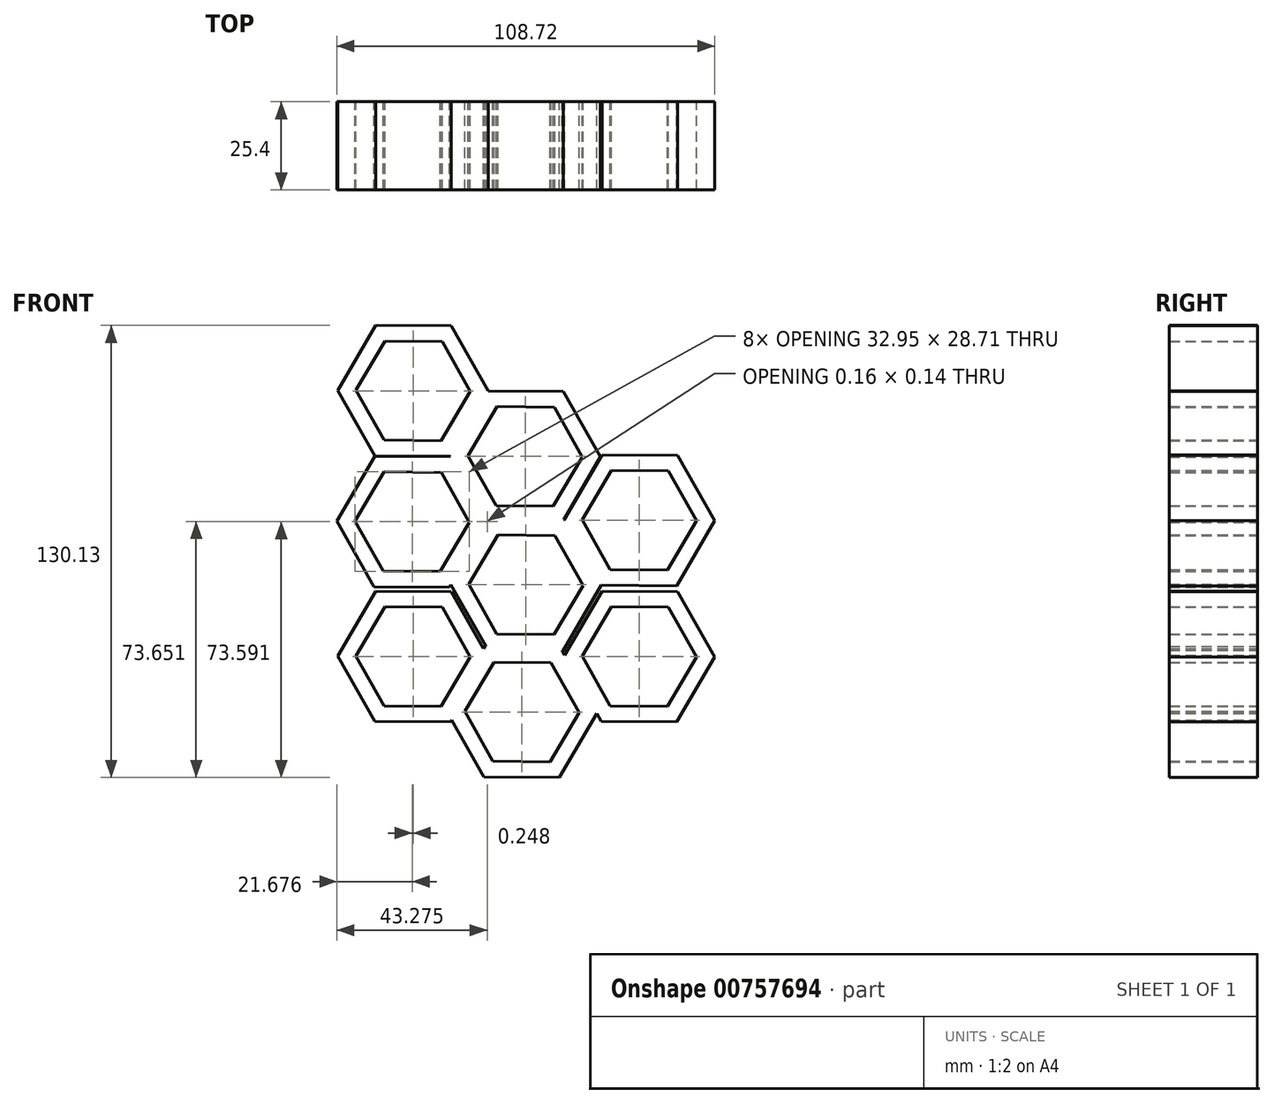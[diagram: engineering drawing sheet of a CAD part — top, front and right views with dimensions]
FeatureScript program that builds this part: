
annotation { "Feature Type Name" : "Feature", "Feature Type Description" : "" }
export const myFeature = defineFeature(function(context is Context, id is Id, definition is map)
    precondition{}
    {
        {
            var Q0;
            Q0=qCreatedBy(makeId("Front.planeOp"),FACE);
            var sketch = newSketch(context, id + "F0", { "sketchPlane" : qUnion([Q0])});
            skCircle(sketch, "E0.cCircle", {"center": v(-59.12, 45.17) * mm, "radius": 18.77 * mm, "construction": true});
            skLineSegment(sketch, "E0.0", {"start": v(-37.45, 45.03) * mm, "end": v(-48.41, 26.33) * mm});
            skLineSegment(sketch, "E0.1", {"start": v(-48.41, 26.33) * mm, "end": v(-70.09, 26.47) * mm});
            skLineSegment(sketch, "E0.2", {"start": v(-70.09, 26.47) * mm, "end": v(-80.8, 45.31) * mm});
            skLineSegment(sketch, "E0.3", {"start": v(-80.8, 45.31) * mm, "end": v(-69.84, 64.01) * mm});
            skLineSegment(sketch, "E0.4", {"start": v(-69.84, 64.01) * mm, "end": v(-48.16, 63.87) * mm});
            skLineSegment(sketch, "E0.5", {"start": v(-48.16, 63.87) * mm, "end": v(-37.45, 45.03) * mm});
            skPoint(sketch, "E0.0.midPoint", {"position": v(-42.93, 35.68) * mm});
            skCircle(sketch, "E1.cCircle", {"center": v(-59.12, 45.17) * mm, "radius": 14.27 * mm, "construction": true});
            skLineSegment(sketch, "E1.0", {"start": v(-42.65, 45) * mm, "end": v(-51.03, 30.82) * mm});
            skLineSegment(sketch, "E1.1", {"start": v(-51.03, 30.82) * mm, "end": v(-67.5, 30.98) * mm});
            skLineSegment(sketch, "E1.2", {"start": v(-67.5, 30.98) * mm, "end": v(-75.6, 45.34) * mm});
            skLineSegment(sketch, "E1.3", {"start": v(-75.6, 45.34) * mm, "end": v(-67.22, 59.52) * mm});
            skLineSegment(sketch, "E1.4", {"start": v(-67.22, 59.52) * mm, "end": v(-50.74, 59.36) * mm});
            skLineSegment(sketch, "E1.5", {"start": v(-50.74, 59.36) * mm, "end": v(-42.65, 45) * mm});
            skPoint(sketch, "E1.0.midPoint", {"position": v(-46.84, 37.91) * mm});
            skCircle(sketch, "E2.cCircle", {"center": v(-26.64, 64) * mm, "radius": 18.77 * mm, "construction": true});
            skLineSegment(sketch, "E2.0", {"start": v(-4.97, 63.86) * mm, "end": v(-15.93, 45.16) * mm});
            skLineSegment(sketch, "E2.1", {"start": v(-15.93, 45.16) * mm, "end": v(-37.6, 45.3) * mm});
            skLineSegment(sketch, "E2.2", {"start": v(-37.6, 45.3) * mm, "end": v(-48.32, 64.14) * mm});
            skLineSegment(sketch, "E2.3", {"start": v(-48.32, 64.14) * mm, "end": v(-37.35, 82.84) * mm});
            skLineSegment(sketch, "E2.4", {"start": v(-37.35, 82.84) * mm, "end": v(-15.68, 82.7) * mm});
            skLineSegment(sketch, "E2.5", {"start": v(-15.68, 82.7) * mm, "end": v(-4.97, 63.86) * mm});
            skPoint(sketch, "E2.0.midPoint", {"position": v(-10.45, 54.5) * mm});
            skCircle(sketch, "E3.cCircle", {"center": v(-26.64, 64) * mm, "radius": 14.27 * mm, "construction": true});
            skLineSegment(sketch, "E3.0", {"start": v(-10.16, 63.83) * mm, "end": v(-18.55, 49.65) * mm});
            skLineSegment(sketch, "E3.1", {"start": v(-18.55, 49.65) * mm, "end": v(-35.02, 49.81) * mm});
            skLineSegment(sketch, "E3.2", {"start": v(-35.02, 49.81) * mm, "end": v(-43.12, 64.17) * mm});
            skLineSegment(sketch, "E3.3", {"start": v(-43.12, 64.17) * mm, "end": v(-34.74, 78.35) * mm});
            skLineSegment(sketch, "E3.4", {"start": v(-34.74, 78.35) * mm, "end": v(-18.26, 78.19) * mm});
            skLineSegment(sketch, "E3.5", {"start": v(-18.26, 78.19) * mm, "end": v(-10.16, 63.83) * mm});
            skPoint(sketch, "E3.0.midPoint", {"position": v(-14.36, 56.74) * mm});
            skCircle(sketch, "E4.cCircle", {"center": v(-26.4, 27.04) * mm, "radius": 18.77 * mm, "construction": true});
            skLineSegment(sketch, "E4.0", {"start": v(-4.72, 26.9) * mm, "end": v(-15.68, 8.2) * mm});
            skLineSegment(sketch, "E4.1", {"start": v(-15.68, 8.2) * mm, "end": v(-37.35, 8.34) * mm});
            skLineSegment(sketch, "E4.2", {"start": v(-37.35, 8.34) * mm, "end": v(-48.07, 27.18) * mm});
            skLineSegment(sketch, "E4.3", {"start": v(-48.07, 27.18) * mm, "end": v(-37.1, 45.88) * mm});
            skLineSegment(sketch, "E4.4", {"start": v(-37.1, 45.88) * mm, "end": v(-15.43, 45.73) * mm});
            skLineSegment(sketch, "E4.5", {"start": v(-15.43, 45.73) * mm, "end": v(-4.72, 26.9) * mm});
            skPoint(sketch, "E4.0.midPoint", {"position": v(-10.2, 17.54) * mm});
            skCircle(sketch, "E5.cCircle", {"center": v(-26.4, 27.04) * mm, "radius": 14.27 * mm, "construction": true});
            skLineSegment(sketch, "E5.0", {"start": v(-9.92, 26.87) * mm, "end": v(-18.3, 12.68) * mm});
            skLineSegment(sketch, "E5.1", {"start": v(-18.3, 12.68) * mm, "end": v(-34.78, 12.85) * mm});
            skLineSegment(sketch, "E5.2", {"start": v(-34.78, 12.85) * mm, "end": v(-42.87, 27.2) * mm});
            skLineSegment(sketch, "E5.3", {"start": v(-42.87, 27.2) * mm, "end": v(-34.49, 41.39) * mm});
            skLineSegment(sketch, "E5.4", {"start": v(-34.49, 41.39) * mm, "end": v(-18, 41.22) * mm});
            skLineSegment(sketch, "E5.5", {"start": v(-18, 41.22) * mm, "end": v(-9.92, 26.87) * mm});
            skPoint(sketch, "E5.0.midPoint", {"position": v(-14.1, 19.78) * mm});
            skCircle(sketch, "E6.cCircle", {"center": v(-58.88, 82.87) * mm, "radius": 18.77 * mm, "construction": true});
            skLineSegment(sketch, "E6.0", {"start": v(-37.2, 82.72) * mm, "end": v(-48.16, 64.02) * mm});
            skLineSegment(sketch, "E6.1", {"start": v(-48.16, 64.02) * mm, "end": v(-69.84, 64.17) * mm});
            skLineSegment(sketch, "E6.2", {"start": v(-69.84, 64.17) * mm, "end": v(-80.55, 83) * mm});
            skLineSegment(sketch, "E6.3", {"start": v(-80.55, 83) * mm, "end": v(-69.59, 101.7) * mm});
            skLineSegment(sketch, "E6.4", {"start": v(-69.59, 101.7) * mm, "end": v(-47.91, 101.57) * mm});
            skLineSegment(sketch, "E6.5", {"start": v(-47.91, 101.57) * mm, "end": v(-37.2, 82.72) * mm});
            skPoint(sketch, "E6.0.midPoint", {"position": v(-42.68, 73.37) * mm});
            skCircle(sketch, "E7.cCircle", {"center": v(-58.88, 82.87) * mm, "radius": 14.27 * mm, "construction": true});
            skLineSegment(sketch, "E7.0", {"start": v(-42.4, 82.7) * mm, "end": v(-50.78, 68.51) * mm});
            skLineSegment(sketch, "E7.1", {"start": v(-50.78, 68.51) * mm, "end": v(-67.26, 68.68) * mm});
            skLineSegment(sketch, "E7.2", {"start": v(-67.26, 68.68) * mm, "end": v(-75.35, 83.03) * mm});
            skLineSegment(sketch, "E7.3", {"start": v(-75.35, 83.03) * mm, "end": v(-66.97, 97.22) * mm});
            skLineSegment(sketch, "E7.4", {"start": v(-66.97, 97.22) * mm, "end": v(-50.5, 97.05) * mm});
            skLineSegment(sketch, "E7.5", {"start": v(-50.5, 97.05) * mm, "end": v(-42.4, 82.7) * mm});
            skPoint(sketch, "E7.0.midPoint", {"position": v(-46.6, 75.6) * mm});
            skCircle(sketch, "E8.cCircle", {"center": v(6.24, 45.6) * mm, "radius": 18.77 * mm, "construction": true});
            skLineSegment(sketch, "E8.0", {"start": v(27.92, 45.45) * mm, "end": v(16.96, 26.75) * mm});
            skLineSegment(sketch, "E8.1", {"start": v(16.96, 26.75) * mm, "end": v(-4.72, 26.9) * mm});
            skLineSegment(sketch, "E8.2", {"start": v(-4.72, 26.9) * mm, "end": v(-15.43, 45.73) * mm});
            skLineSegment(sketch, "E8.3", {"start": v(-15.43, 45.73) * mm, "end": v(-4.47, 64.43) * mm});
            skLineSegment(sketch, "E8.4", {"start": v(-4.47, 64.43) * mm, "end": v(17.2, 64.3) * mm});
            skLineSegment(sketch, "E8.5", {"start": v(17.2, 64.3) * mm, "end": v(27.92, 45.45) * mm});
            skPoint(sketch, "E8.0.midPoint", {"position": v(22.44, 36.1) * mm});
            skCircle(sketch, "E9.cCircle", {"center": v(6.24, 45.6) * mm, "radius": 14.27 * mm, "construction": true});
            skLineSegment(sketch, "E9.0", {"start": v(22.72, 45.42) * mm, "end": v(14.34, 31.24) * mm});
            skLineSegment(sketch, "E9.1", {"start": v(14.34, 31.24) * mm, "end": v(-2.14, 31.4) * mm});
            skLineSegment(sketch, "E9.2", {"start": v(-2.14, 31.4) * mm, "end": v(-10.23, 45.76) * mm});
            skLineSegment(sketch, "E9.3", {"start": v(-10.23, 45.76) * mm, "end": v(-1.85, 59.94) * mm});
            skLineSegment(sketch, "E9.4", {"start": v(-1.85, 59.94) * mm, "end": v(14.63, 59.78) * mm});
            skLineSegment(sketch, "E9.5", {"start": v(14.63, 59.78) * mm, "end": v(22.72, 45.42) * mm});
            skPoint(sketch, "E9.0.midPoint", {"position": v(18.53, 38.33) * mm});
            skCircle(sketch, "E10.cCircle", {"center": v(-58.88, 6.38) * mm, "radius": 18.77 * mm, "construction": true});
            skLineSegment(sketch, "E10.0", {"start": v(-37.2, 6.23) * mm, "end": v(-48.16, -12.47) * mm});
            skLineSegment(sketch, "E10.1", {"start": v(-48.16, -12.47) * mm, "end": v(-69.84, -12.32) * mm});
            skLineSegment(sketch, "E10.2", {"start": v(-69.84, -12.32) * mm, "end": v(-80.55, 6.52) * mm});
            skLineSegment(sketch, "E10.3", {"start": v(-80.55, 6.52) * mm, "end": v(-69.59, 25.22) * mm});
            skLineSegment(sketch, "E10.4", {"start": v(-69.59, 25.22) * mm, "end": v(-47.91, 25.08) * mm});
            skLineSegment(sketch, "E10.5", {"start": v(-47.91, 25.08) * mm, "end": v(-37.2, 6.23) * mm});
            skPoint(sketch, "E10.0.midPoint", {"position": v(-42.68, -3.12) * mm});
            skCircle(sketch, "E11.cCircle", {"center": v(-58.88, 6.38) * mm, "radius": 14.27 * mm, "construction": true});
            skLineSegment(sketch, "E11.0", {"start": v(-42.4, 6.2) * mm, "end": v(-50.78, -7.98) * mm});
            skLineSegment(sketch, "E11.1", {"start": v(-50.78, -7.98) * mm, "end": v(-67.26, -7.81) * mm});
            skLineSegment(sketch, "E11.2", {"start": v(-67.26, -7.81) * mm, "end": v(-75.35, 6.54) * mm});
            skLineSegment(sketch, "E11.3", {"start": v(-75.35, 6.54) * mm, "end": v(-66.97, 20.73) * mm});
            skLineSegment(sketch, "E11.4", {"start": v(-66.97, 20.73) * mm, "end": v(-50.5, 20.56) * mm});
            skLineSegment(sketch, "E11.5", {"start": v(-50.5, 20.56) * mm, "end": v(-42.4, 6.2) * mm});
            skPoint(sketch, "E11.0.midPoint", {"position": v(-46.6, -0.88) * mm});
            skCircle(sketch, "E12.cCircle", {"center": v(6.24, 6.38) * mm, "radius": 18.77 * mm, "construction": true});
            skLineSegment(sketch, "E12.0", {"start": v(27.92, 6.23) * mm, "end": v(16.96, -12.47) * mm});
            skLineSegment(sketch, "E12.1", {"start": v(16.96, -12.47) * mm, "end": v(-4.72, -12.32) * mm});
            skLineSegment(sketch, "E12.2", {"start": v(-4.72, -12.32) * mm, "end": v(-15.43, 6.52) * mm});
            skLineSegment(sketch, "E12.3", {"start": v(-15.43, 6.52) * mm, "end": v(-4.47, 25.22) * mm});
            skLineSegment(sketch, "E12.4", {"start": v(-4.47, 25.22) * mm, "end": v(17.2, 25.08) * mm});
            skLineSegment(sketch, "E12.5", {"start": v(17.2, 25.08) * mm, "end": v(27.92, 6.23) * mm});
            skPoint(sketch, "E12.0.midPoint", {"position": v(22.44, -3.12) * mm});
            skCircle(sketch, "E13.cCircle", {"center": v(6.24, 6.38) * mm, "radius": 14.27 * mm, "construction": true});
            skLineSegment(sketch, "E13.0", {"start": v(22.72, 6.2) * mm, "end": v(14.34, -7.98) * mm});
            skLineSegment(sketch, "E13.1", {"start": v(14.34, -7.98) * mm, "end": v(-2.14, -7.81) * mm});
            skLineSegment(sketch, "E13.2", {"start": v(-2.14, -7.81) * mm, "end": v(-10.23, 6.54) * mm});
            skLineSegment(sketch, "E13.3", {"start": v(-10.23, 6.54) * mm, "end": v(-1.85, 20.73) * mm});
            skLineSegment(sketch, "E13.4", {"start": v(-1.85, 20.73) * mm, "end": v(14.63, 20.56) * mm});
            skLineSegment(sketch, "E13.5", {"start": v(14.63, 20.56) * mm, "end": v(22.72, 6.2) * mm});
            skPoint(sketch, "E13.0.midPoint", {"position": v(18.53, -0.88) * mm});
            skCircle(sketch, "E14.cCircle", {"center": v(-27.54, -9.58) * mm, "radius": 18.77 * mm, "construction": true});
            skLineSegment(sketch, "E14.0", {"start": v(-5.87, -9.72) * mm, "end": v(-16.83, -28.42) * mm});
            skLineSegment(sketch, "E14.1", {"start": v(-16.83, -28.42) * mm, "end": v(-38.5, -28.28) * mm});
            skLineSegment(sketch, "E14.2", {"start": v(-38.5, -28.28) * mm, "end": v(-49.22, -9.43) * mm});
            skLineSegment(sketch, "E14.3", {"start": v(-49.22, -9.43) * mm, "end": v(-38.26, 9.27) * mm});
            skLineSegment(sketch, "E14.4", {"start": v(-38.26, 9.27) * mm, "end": v(-16.58, 9.12) * mm});
            skLineSegment(sketch, "E14.5", {"start": v(-16.58, 9.12) * mm, "end": v(-5.87, -9.72) * mm});
            skPoint(sketch, "E14.0.midPoint", {"position": v(-11.35, -19.07) * mm});
            skCircle(sketch, "E15.cCircle", {"center": v(-27.54, -9.58) * mm, "radius": 14.27 * mm, "construction": true});
            skLineSegment(sketch, "E15.0", {"start": v(-11.07, -9.74) * mm, "end": v(-19.45, -23.93) * mm});
            skLineSegment(sketch, "E15.1", {"start": v(-19.45, -23.93) * mm, "end": v(-35.93, -23.76) * mm});
            skLineSegment(sketch, "E15.2", {"start": v(-35.93, -23.76) * mm, "end": v(-44.02, -9.4) * mm});
            skLineSegment(sketch, "E15.3", {"start": v(-44.02, -9.4) * mm, "end": v(-35.64, 4.78) * mm});
            skLineSegment(sketch, "E15.4", {"start": v(-35.64, 4.78) * mm, "end": v(-19.16, 4.61) * mm});
            skLineSegment(sketch, "E15.5", {"start": v(-19.16, 4.61) * mm, "end": v(-11.07, -9.74) * mm});
            skPoint(sketch, "E15.0.midPoint", {"position": v(-15.26, -16.84) * mm});
            skSolve(sketch);
        }
        {
            var Q0;
            Q0 = qSketchRegion(id + "F0", true);
            extrude(context, id + "F1", {"entities" : qUnion([Q0]), "depth" : 25.4 * mm, "offsetDistance" : 25.4 * mm});
        }
    });
